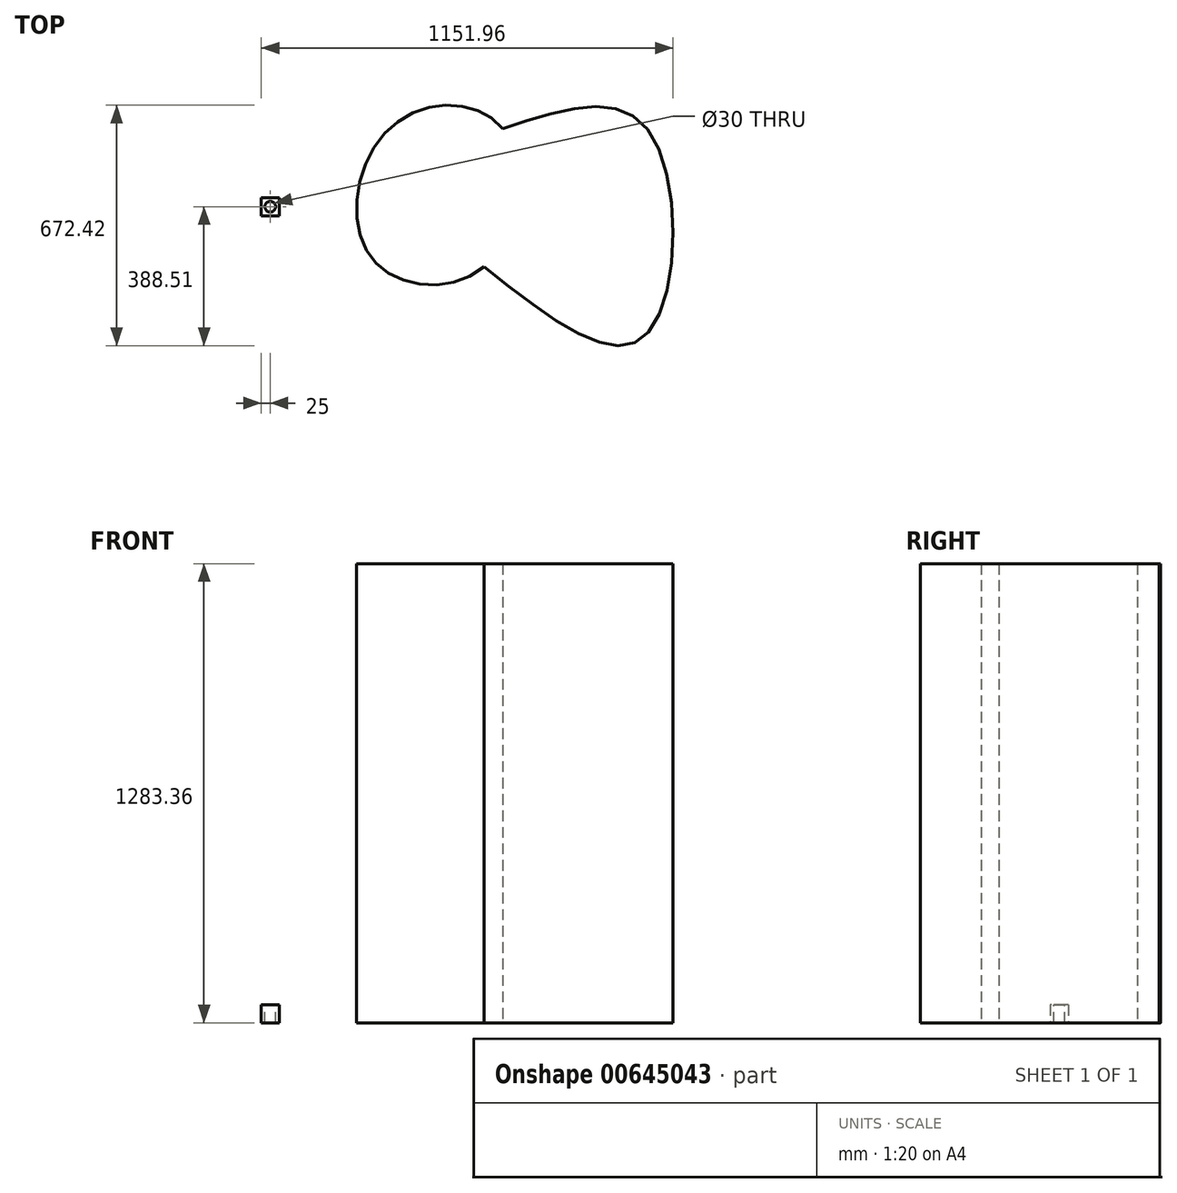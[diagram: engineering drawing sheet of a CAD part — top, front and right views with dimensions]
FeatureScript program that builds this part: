
annotation { "Feature Type Name" : "Feature", "Feature Type Description" : "" }
export const myFeature = defineFeature(function(context is Context, id is Id, definition is map)
    precondition{}
    {
        {
            var Q0;
            Q0=qCreatedBy(makeId("Top.planeOp"),FACE);
            var sketch = newSketch(context, id + "F0", { "sketchPlane" : qUnion([Q0])});
            skLineSegment(sketch, "E0.bottom", {"start": v(25, 25) * mm, "end": v(-25, 25) * mm});
            skLineSegment(sketch, "E0.top", {"start": v(25, -25) * mm, "end": v(-25, -25) * mm});
            skLineSegment(sketch, "E0.left", {"start": v(25, 25) * mm, "end": v(25, -25) * mm});
            skLineSegment(sketch, "E0.right", {"start": v(-25, 25) * mm, "end": v(-25, -25) * mm});
            skPoint(sketch, "E0.middle", {"position": v(0, 0) * mm});
            skSolve(sketch);
        }
        {
            var Q0;
            Q0 = qSketchRegion(id + "F0", true);
            extrude(context, id + "F1", {"entities" : qUnion([Q0]), "depth" : 50 * mm, "offsetDistance" : 25 * mm});
        }
        {
            var Q0;
            Q0=makeQuery(id+"F1.opExtrude","CAP_FACE",FACE,{"disambiguationData":[OSD([sQuery(id+"F0.wireOp",EDGE,"E0.bottom"),sQuery(id+"F0.wireOp",EDGE,"E0.top"),sQuery(id+"F0.wireOp",EDGE,"E0.left"),sQuery(id+"F0.wireOp",EDGE,"E0.right")])],"isStart":false});
            var sketch = newSketch(context, id + "F2", { "sketchPlane" : qUnion([Q0])});
            skCircle(sketch, "E1", {"center": v(0, 0) * mm, "radius": 15 * mm});
            skSolve(sketch);
        }
        {
            var Q0;
            Q0 = qSketchRegion(id + "F2", true);
            extrude(context, id + "F3", {"entities" : qUnion([Q0]), "operationType" : NewBodyOperationType.REMOVE, "oppositeDirection" : true, "depth" : 50 * mm, "offsetDistance" : 25 * mm});
        }
        {
            var Q0;
            Q0=qCreatedBy(makeId("Top.planeOp"),FACE);
            var sketch = newSketch(context, id + "F4", { "sketchPlane" : qUnion([Q0])});
            skFitSpline(sketch, "E2", {"points": [v(341.77, 226.2) * mm, v(280.7, -140.36) * mm, v(598.17, -168.22) * mm, v(650.25, 218.1) * mm, v(341.77, 226.2) * mm]});
            skFitSpline(sketch, "E3", {"points": [v(598.17, -168.22) * mm, v(1045.63, -362.7) * mm, v(1054.36, 218.1) * mm, v(650.25, 218.1) * mm], "startDerivative": vector(1587.23, -1257.3) * mm, "endDerivative": vector(-1580.52, -530.39) * mm});
            skSolve(sketch);
        }
        {
            var Q0;
            {var subQ0=sQuery(id+"F4.wireOp",EDGE,"E3");Q0=makeQuery(id+"F4.imprint","IMPRINT",FACE,{"disambiguationData":[TD([[makeQuery(id+"F4.imprint","IMPRINT",EDGE,{"derivedFrom":subQ0}),1.0]])]});}
            var Q1;
            {var subQ0=sQuery(id+"F4.wireOp",EDGE,"E3");var subQ1=sQuery(id+"F4.wireOp",EDGE,"E2");var subQ2=makeQuery(id+"F4.imprint","INTERSECT",VERTEX,{"disambiguationData":[OD(0.0)],"derivedFrom":[subQ1,subQ0]});Q1=makeQuery(id+"F4.imprint","IMPRINT",FACE,{"disambiguationData":[TD([[makeQuery(id+"F4.imprint","IMPRINT",EDGE,{"disambiguationData":[TD([[subQ2,-1.0]])],"derivedFrom":subQ1}),1.0]])]});}
            extrude(context, id + "F5", {"entities" : qUnion([Q0, Q1]), "depth" : 1283.36 * mm, "offsetDistance" : 25 * mm});
        }
    });
